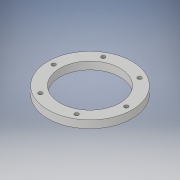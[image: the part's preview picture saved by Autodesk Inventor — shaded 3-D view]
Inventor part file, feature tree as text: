
AUTODESK INVENTOR PART (.ipt)
format: ipt  version: 2019 (Build 230136000, 136)  size: 118,784 bytes
history: native  units: in
note: dims shown in document units (in); Inventor stores cm internally (conversion verified against a paired STEP export)
features: sketch x2, extrude x1, hole x1
ambient origin geometry x8: Origin, YZ Plane, XZ Plane, XY Plane, X Axis, Y Axis, Z Axis, Center Point
bodies: Solid1 (feature_tree)
feature tree (4):
  extrude  "Extrusion1"  Depth=3.937in
  hole  "Hole1"  [1 undecoded]
  sketch  "Sketch1"  dims[d0=5.5in d1=3.937in]
  sketch  "Sketch2"  dims[d2=0.5in d3=0.0in d4=0.375in d5=2.3622in d7=360.0deg d9=0.257in d10=0.75in d11=0.438in d12=0.25in d13=0.5635in d14=0.484in d15=0.0in]
note: 1 required parameter value undecoded (feature->parameter linkage not recoverable at this tier; creation-order binding heuristic only, values carry confidence <= 0.55)
